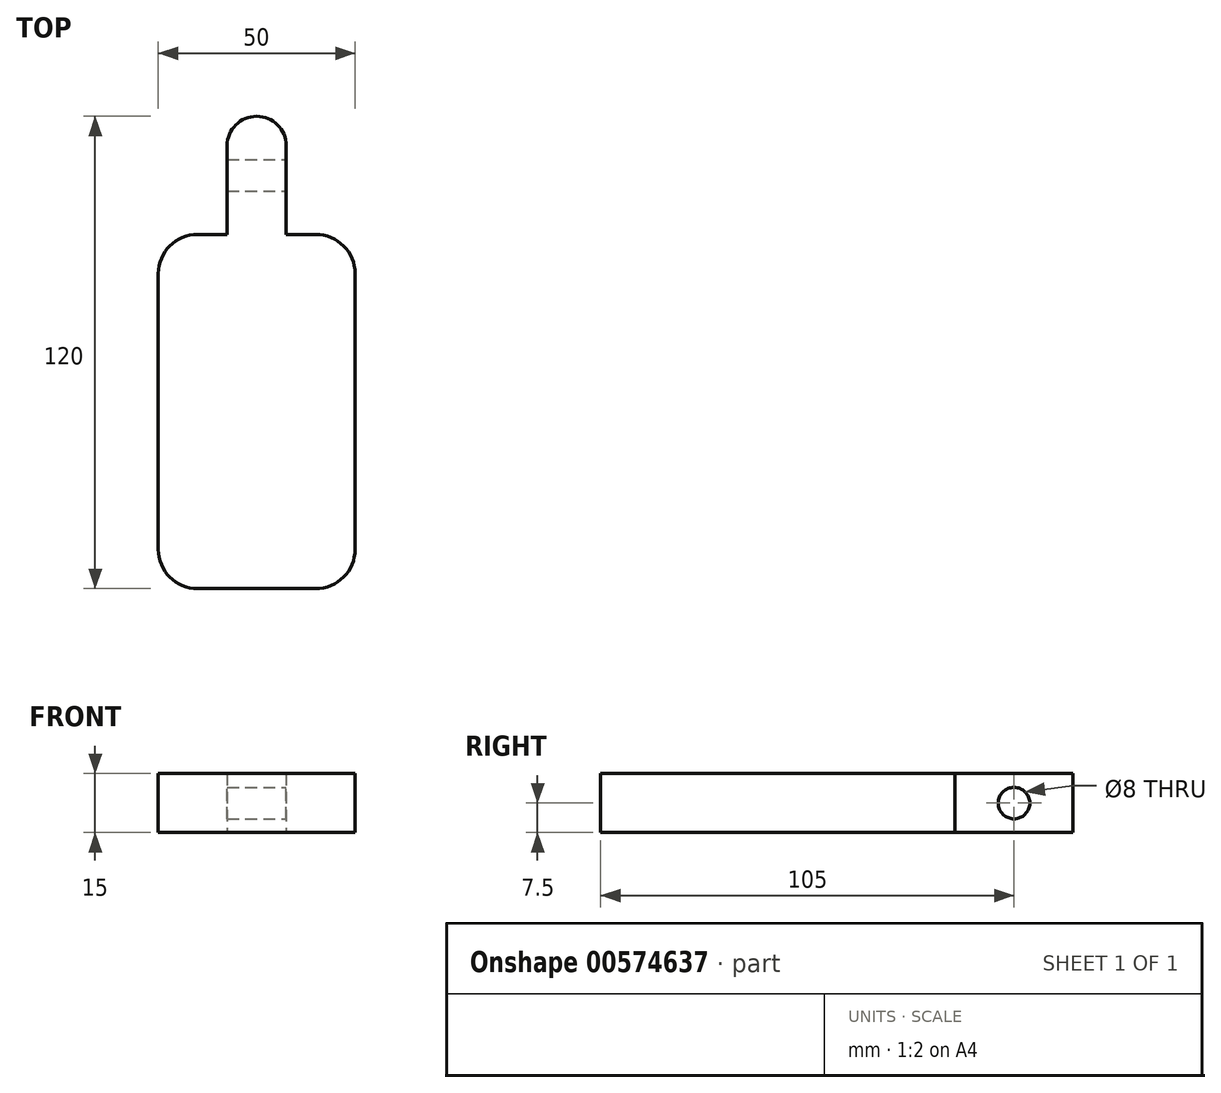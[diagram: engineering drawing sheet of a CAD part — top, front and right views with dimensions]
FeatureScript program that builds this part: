
annotation { "Feature Type Name" : "Feature", "Feature Type Description" : "" }
export const myFeature = defineFeature(function(context is Context, id is Id, definition is map)
    precondition{}
    {
        {
            var Q0;
            Q0=qCreatedBy(makeId("Top.planeOp"),FACE);
            var sketch = newSketch(context, id + "F0", { "sketchPlane" : qUnion([Q0])});
            skLineSegment(sketch, "E0.bottom", {"start": v(0, 0) * mm, "end": v(50, 0) * mm});
            skLineSegment(sketch, "E0.top", {"start": v(0, 90) * mm, "end": v(17.5, 90) * mm});
            skLineSegment(sketch, "E0.left", {"start": v(0, 0) * mm, "end": v(0, 90) * mm});
            skLineSegment(sketch, "E0.right", {"start": v(50, 0) * mm, "end": v(50, 90) * mm});
            skLineSegment(sketch, "E1", {"start": v(17.5, 90) * mm, "end": v(17.5, 120) * mm});
            skLineSegment(sketch, "E2", {"start": v(32.5, 90) * mm, "end": v(32.5, 120) * mm});
            skLineSegment(sketch, "E3", {"start": v(17.5, 120) * mm, "end": v(32.5, 120) * mm});
            skLineSegment(sketch, "E4.trimOffspring", {"start": v(32.5, 90) * mm, "end": v(50, 90) * mm});
            skSolve(sketch);
        }
        {
            var Q0;
            Q0 = qSketchRegion(id + "F0", true);
            extrude(context, id + "F1", {"entities" : qUnion([Q0]), "depth" : 15 * mm, "offsetDistance" : 25 * mm});
        }
        {
            var Q0;
            Q0=makeQuery(id+"F1.opExtrude","SWEPT_EDGE",EDGE,{"disambiguationData":[OSD([sQuery(id+"F0.wireOp",EDGE,"E1"),sQuery(id+"F0.wireOp",EDGE,"E3")])]});
            var Q1;
            Q1=makeQuery(id+"F1.opExtrude","SWEPT_EDGE",EDGE,{"disambiguationData":[OSD([sQuery(id+"F0.wireOp",EDGE,"E2"),sQuery(id+"F0.wireOp",EDGE,"E3")])]});
            fillet(context, id + "F2", {"entities" : qUnion([Q0, Q1]), "radius" : 7.5 * mm, "tangentPropagation" : true, "allowEdgeOverflow" : false});
        }
        {
            var Q0;
            Q0=makeQuery(id+"F1.opExtrude","SWEPT_EDGE",EDGE,{"disambiguationData":[OSD([sQuery(id+"F0.wireOp",EDGE,"E0.top"),sQuery(id+"F0.wireOp",EDGE,"E0.left")])]});
            var Q1;
            Q1=makeQuery(id+"F1.opExtrude","SWEPT_EDGE",EDGE,{"disambiguationData":[OSD([sQuery(id+"F0.wireOp",EDGE,"E0.right"),sQuery(id+"F0.wireOp",EDGE,"E4.trimOffspring")])]});
            var Q2;
            Q2=makeQuery(id+"F1.opExtrude","SWEPT_EDGE",EDGE,{"disambiguationData":[OSD([sQuery(id+"F0.wireOp",EDGE,"E0.bottom"),sQuery(id+"F0.wireOp",EDGE,"E0.right")])]});
            var Q3;
            Q3=makeQuery(id+"F1.opExtrude","SWEPT_EDGE",EDGE,{"disambiguationData":[OSD([sQuery(id+"F0.wireOp",EDGE,"E0.bottom"),sQuery(id+"F0.wireOp",EDGE,"E0.left")])]});
            fillet(context, id + "F3", {"entities" : qUnion([Q0, Q1, Q2, Q3]), "radius" : 10 * mm, "tangentPropagation" : true, "allowEdgeOverflow" : false});
        }
        {
            var Q0;
            Q0=makeQuery(id+"F1.opExtrude","SWEPT_FACE",FACE,{"disambiguationData":[OSD([sQuery(id+"F0.wireOp",EDGE,"E2")])]});
            var sketch = newSketch(context, id + "F4", { "sketchPlane" : qUnion([Q0])});
            skPoint(sketch, "E5.centerSnap0", {"position": v(112.5, 7.5) * mm});
            skPoint(sketch, "E5.centerSnap1", {"position": v(101.25, 0) * mm});
            skCircle(sketch, "E6", {"center": v(105, 7.5) * mm, "radius": 4 * mm});
            skSolve(sketch);
        }
        {
            var Q0;
            Q0=makeQuery(id+"F4.imprint","IMPRINT",FACE,{"disambiguationData":[TD([[makeQuery(id+"F4.imprint","IMPRINT",EDGE,{"derivedFrom":sQuery(id+"F4.wireOp",EDGE,"E6")}),1.0]])]});
            extrude(context, id + "F5", {"entities" : qUnion([Q0]), "operationType" : NewBodyOperationType.REMOVE, "oppositeDirection" : true, "depth" : 15 * mm, "offsetDistance" : 25 * mm});
        }
    });
